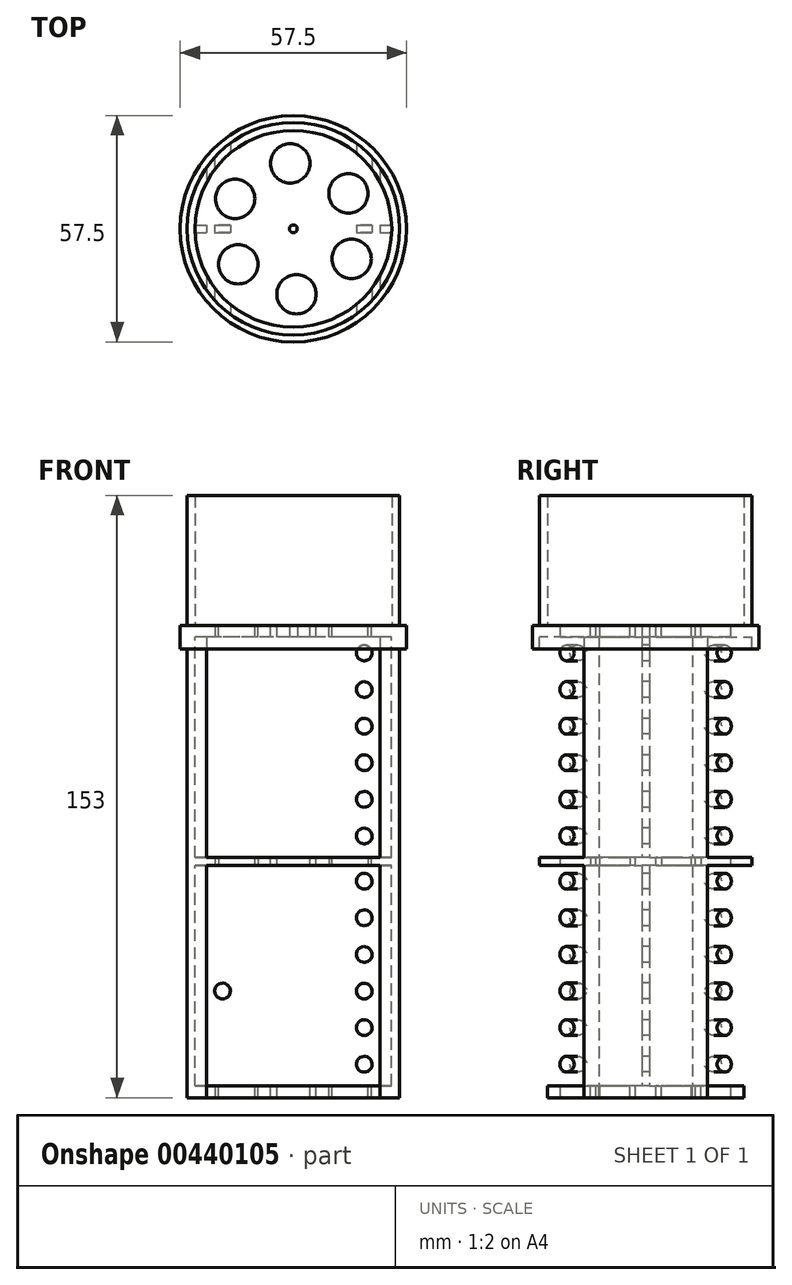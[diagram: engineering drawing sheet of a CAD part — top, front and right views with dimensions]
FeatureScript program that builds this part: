
annotation { "Feature Type Name" : "Feature", "Feature Type Description" : "" }
export const myFeature = defineFeature(function(context is Context, id is Id, definition is map)
    precondition{}
    {
        {
            var Q0;
            Q0=qCreatedBy(makeId("Top.planeOp"),FACE);
            var sketch = newSketch(context, id + "F0", { "sketchPlane" : qUnion([Q0])});
            skCircle(sketch, "E0", {"center": v(0, 0) * mm, "radius": 28.75 * mm});
            skCircle(sketch, "E1", {"center": v(0, 0) * mm, "radius": 27 * mm});
            skCircle(sketch, "E2", {"center": v(0, 0) * mm, "radius": 25 * mm});
            skLineSegment(sketch, "E3", {"start": v(0, 0) * mm, "end": v(28.75, 0) * mm, "construction": true});
            skLineSegment(sketch, "E4", {"start": v(0, 0) * mm, "end": v(-14.37, 24.9) * mm, "construction": true});
            skLineSegment(sketch, "E5", {"start": v(0, 0) * mm, "end": v(-14.38, -24.9) * mm, "construction": true});
            skCircle(sketch, "E6", {"center": v(14, 9) * mm, "radius": 5 * mm});
            skCircle(sketch, "E7", {"center": v(-14, -9) * mm, "radius": 5 * mm});
            skCircle(sketch, "E8.1.0", {"center": v(14.8, -7.62) * mm, "radius": 5 * mm});
            skCircle(sketch, "E8.2.0", {"center": v(0.8, -16.62) * mm, "radius": 5 * mm});
            skCircle(sketch, "E8.4.0", {"center": v(-14.8, 7.62) * mm, "radius": 5 * mm});
            skCircle(sketch, "E8.5.0", {"center": v(-0.8, 16.62) * mm, "radius": 5 * mm});
            skSolve(sketch);
        }
        {
            var Q0;
            Q0=qCreatedBy(makeId("Top.planeOp"),FACE);
            var sketch = newSketch(context, id + "F1", { "sketchPlane" : qUnion([Q0])});
            skArc(sketch, "E9.0.0", {"start": v(-24.98, 1) * mm, "mid": v(-25, 0) * mm, "end": v(-24.98, -1) * mm});
            skLineSegment(sketch, "E10", {"start": v(24.98, 1) * mm, "end": v(-24.98, 1) * mm});
            skLineSegment(sketch, "E11", {"start": v(24.98, -1) * mm, "end": v(-24.98, -1) * mm});
            skArc(sketch, "E12.trimOffspring", {"start": v(24.98, -1) * mm, "mid": v(25, 0) * mm, "end": v(24.98, 1) * mm});
            skSolve(sketch);
        }
        {
            var Q0;
            Q0=qCreatedBy(makeId("Front.planeOp"),FACE);
            var sketch = newSketch(context, id + "F2", { "sketchPlane" : qUnion([Q0])});
            skLineSegment(sketch, "E13", {"start": v(0, 0) * mm, "end": v(25, 0) * mm, "construction": true});
            skLineSegment(sketch, "E14", {"start": v(25, 0) * mm, "end": v(27, 0) * mm, "construction": true});
            skLineSegment(sketch, "E15", {"start": v(27, 0) * mm, "end": v(28.75, 0) * mm, "construction": true});
            skLineSegment(sketch, "E16", {"start": v(25, -10) * mm, "end": v(25, 10) * mm, "construction": true});
            skLineSegment(sketch, "E17", {"start": v(27, -10) * mm, "end": v(27, 10) * mm, "construction": true});
            skLineSegment(sketch, "E18", {"start": v(28.75, -10) * mm, "end": v(28.75, 10) * mm, "construction": true});
            skLineSegment(sketch, "E19", {"start": v(25, 10) * mm, "end": v(25, 105) * mm, "construction": true});
            skLineSegment(sketch, "E20", {"start": v(27, 10) * mm, "end": v(27, 105) * mm, "construction": true});
            skLineSegment(sketch, "E21", {"start": v(25, -10) * mm, "end": v(25, -105) * mm, "construction": true});
            skLineSegment(sketch, "E22", {"start": v(27, -10) * mm, "end": v(27, -105) * mm, "construction": true});
            skLineSegment(sketch, "E23", {"start": v(0, 0) * mm, "end": v(-25, 0) * mm, "construction": true});
            skLineSegment(sketch, "E24", {"start": v(-25, 0) * mm, "end": v(-27, 0) * mm, "construction": true});
            skLineSegment(sketch, "E25", {"start": v(-27, 0) * mm, "end": v(-28.75, 0) * mm, "construction": true});
            skLineSegment(sketch, "E26", {"start": v(0, 0) * mm, "end": v(0, 43) * mm, "construction": true});
            skLineSegment(sketch, "E27", {"start": v(0, 43) * mm, "end": v(0, 45) * mm, "construction": true});
            skLineSegment(sketch, "E28", {"start": v(0, 0) * mm, "end": v(0, -13) * mm, "construction": true});
            skLineSegment(sketch, "E29", {"start": v(0, -13) * mm, "end": v(0, -15) * mm, "construction": true});
            skLineSegment(sketch, "E30", {"start": v(0, 45) * mm, "end": v(0, 101) * mm, "construction": true});
            skLineSegment(sketch, "E31", {"start": v(0, -15) * mm, "end": v(0, -101) * mm, "construction": true});
            skLineSegment(sketch, "E32", {"start": v(0, 101) * mm, "end": v(0, 105) * mm, "construction": true});
            skLineSegment(sketch, "E33", {"start": v(0, -101) * mm, "end": v(0, -105) * mm, "construction": true});
            skLineSegment(sketch, "E34.bottom", {"start": v(-22, 101) * mm, "end": v(22, 101) * mm});
            skLineSegment(sketch, "E34.top", {"start": v(-22, 45) * mm, "end": v(22, 45) * mm});
            skLineSegment(sketch, "E34.left", {"start": v(-22, 101) * mm, "end": v(-22, 45) * mm});
            skLineSegment(sketch, "E34.right", {"start": v(22, 101) * mm, "end": v(22, 45) * mm});
            skLineSegment(sketch, "E35.bottom", {"start": v(-22, 43) * mm, "end": v(22, 43) * mm});
            skLineSegment(sketch, "E35.top", {"start": v(-22, -13) * mm, "end": v(22, -13) * mm});
            skLineSegment(sketch, "E35.left", {"start": v(-22, 43) * mm, "end": v(-22, -13) * mm});
            skLineSegment(sketch, "E35.right", {"start": v(22, 43) * mm, "end": v(22, -13) * mm});
            skLineSegment(sketch, "E36.bottom", {"start": v(-22, -15) * mm, "end": v(22, -15) * mm});
            skLineSegment(sketch, "E36.top", {"start": v(-22, -101) * mm, "end": v(22, -101) * mm});
            skLineSegment(sketch, "E36.left", {"start": v(-22, -15) * mm, "end": v(-22, -101) * mm});
            skLineSegment(sketch, "E36.right", {"start": v(22, -15) * mm, "end": v(22, -101) * mm});
            skLineSegment(sketch, "E37", {"start": v(-22, 10) * mm, "end": v(22, 10) * mm});
            skSolve(sketch);
        }
        {
            var Q0;
            Q0=sQuery(id+"F2.wireOp",VERTEX,"E35.bottom.end");
            var Q1;
            Q1=qCreatedBy(makeId("Top.planeOp"),FACE);
            cPlane(context, id + "F3", {"entities" : qUnion([Q0, Q1]), "cplaneType" : CPlaneType.PLANE_POINT, "offset" : 25 * mm, "width" : 150 * mm, "height" : 150 * mm});
        }
        {
            var Q0;
            Q0=sQuery(id+"F2.wireOp",VERTEX,"E34.bottom.end");
            var Q1;
            Q1=qCreatedBy(id+"F3.planeOp",FACE);
            cPlane(context, id + "F4", {"entities" : qUnion([Q0, Q1]), "cplaneType" : CPlaneType.PLANE_POINT, "offset" : 25 * mm, "width" : 150 * mm, "height" : 150 * mm});
        }
        {
            var Q0;
            Q0=sQuery(id+"F2.wireOp",VERTEX,"E35.right.end");
            var Q1;
            Q1=qCreatedBy(makeId("Top.planeOp"),FACE);
            cPlane(context, id + "F5", {"entities" : qUnion([Q0, Q1]), "cplaneType" : CPlaneType.PLANE_POINT, "offset" : 25 * mm, "width" : 150 * mm, "height" : 150 * mm});
        }
        {
            var Q0;
            Q0=sQuery(id+"F2.wireOp",VERTEX,"E36.top.end");
            var Q1;
            Q1=qCreatedBy(id+"F5.planeOp",FACE);
            cPlane(context, id + "F6", {"entities" : qUnion([Q0, Q1]), "cplaneType" : CPlaneType.PLANE_POINT, "offset" : 25 * mm, "width" : 150 * mm, "height" : 150 * mm});
        }
        {
            var Q0;
            Q0=qCreatedBy(id+"F5.planeOp",FACE);
            var sketch = newSketch(context, id + "F7", { "sketchPlane" : qUnion([Q0])});
            skCircle(sketch, "E38.0", {"center": v(0, 0) * mm, "radius": 25 * mm});
            skLineSegment(sketch, "E39", {"start": v(0, 0) * mm, "end": v(14, 0) * mm, "construction": true});
            skLineSegment(sketch, "E40", {"start": v(14, 0) * mm, "end": v(14, 9) * mm, "construction": true});
            skLineSegment(sketch, "E41", {"start": v(0, 0) * mm, "end": v(-14, 0) * mm, "construction": true});
            skLineSegment(sketch, "E42", {"start": v(-14, 0) * mm, "end": v(-14, -9) * mm, "construction": true});
            skCircle(sketch, "E43", {"center": v(14, 9) * mm, "radius": 5 * mm});
            skCircle(sketch, "E44", {"center": v(-14, -9) * mm, "radius": 5 * mm});
            skSolve(sketch);
        }
        {
            var Q0;
            Q0=qCreatedBy(id+"F3.planeOp",FACE);
            var sketch = newSketch(context, id + "F8", { "sketchPlane" : qUnion([Q0])});
            skCircle(sketch, "E45.0.0", {"center": v(0, 0) * mm, "radius": 25 * mm});
            skCircle(sketch, "E46.0", {"center": v(14, 9) * mm, "radius": 5 * mm});
            skCircle(sketch, "E46.1", {"center": v(-14, -9) * mm, "radius": 5 * mm});
            skSolve(sketch);
        }
        {
            var Q0;
            Q0=qCreatedBy(id+"F4.planeOp",FACE);
            var sketch = newSketch(context, id + "F9", { "sketchPlane" : qUnion([Q0])});
            skCircle(sketch, "E47.0", {"center": v(0, 0) * mm, "radius": 25 * mm});
            skCircle(sketch, "E48", {"center": v(0, 0) * mm, "radius": 1 * mm});
            skCircle(sketch, "E49.0", {"center": v(0, 0) * mm, "radius": 27 * mm});
            skCircle(sketch, "E50.0", {"center": v(0, 0) * mm, "radius": 28.75 * mm});
            skSolve(sketch);
        }
        {
            var Q0;
            Q0=qCreatedBy(makeId("Front.planeOp"),FACE);
            var sketch = newSketch(context, id + "F10", { "sketchPlane" : qUnion([Q0])});
            skLineSegment(sketch, "E51.0.0", {"start": v(-22, 101) * mm, "end": v(-22, 45) * mm});
            skLineSegment(sketch, "E51.0.1", {"start": v(-22, 45) * mm, "end": v(22, 45) * mm});
            skLineSegment(sketch, "E51.0.2", {"start": v(22, 45) * mm, "end": v(22, 101) * mm});
            skLineSegment(sketch, "E51.0.3", {"start": v(22, 101) * mm, "end": v(-22, 101) * mm});
            skLineSegment(sketch, "E51.1.0", {"start": v(-22, 43) * mm, "end": v(-22, 10) * mm});
            skLineSegment(sketch, "E51.1.1", {"start": v(-22, 10) * mm, "end": v(22, 10) * mm});
            skLineSegment(sketch, "E51.1.2", {"start": v(22, 10) * mm, "end": v(22, 43) * mm});
            skLineSegment(sketch, "E51.1.3", {"start": v(22, 43) * mm, "end": v(-22, 43) * mm});
            skLineSegment(sketch, "E51.2.0", {"start": v(-22, 10) * mm, "end": v(-22, -13) * mm});
            skLineSegment(sketch, "E51.2.1", {"start": v(-22, -13) * mm, "end": v(22, -13) * mm});
            skLineSegment(sketch, "E51.2.2", {"start": v(22, -13) * mm, "end": v(22, 10) * mm});
            skLineSegment(sketch, "E51.2.3", {"start": v(22, 10) * mm, "end": v(-22, 10) * mm});
            skLineSegment(sketch, "E51.3.0", {"start": v(-22, -15) * mm, "end": v(-22, -101) * mm});
            skLineSegment(sketch, "E51.3.1", {"start": v(-22, -101) * mm, "end": v(22, -101) * mm});
            skLineSegment(sketch, "E51.3.2", {"start": v(22, -101) * mm, "end": v(22, -15) * mm});
            skLineSegment(sketch, "E51.3.3", {"start": v(22, -15) * mm, "end": v(-22, -15) * mm});
            skCircle(sketch, "E52", {"center": v(-18, 97) * mm, "radius": 2 * mm});
            skCircle(sketch, "E53.1.0.0", {"center": v(-18, 87.7) * mm, "radius": 2 * mm});
            skCircle(sketch, "E53.2.0.0", {"center": v(-18, 78.4) * mm, "radius": 2 * mm});
            skCircle(sketch, "E53.3.0.0", {"center": v(-18, 69.1) * mm, "radius": 2 * mm});
            skCircle(sketch, "E53.4.0.0", {"center": v(-18, 59.8) * mm, "radius": 2 * mm});
            skCircle(sketch, "E53.5.0.0", {"center": v(-18, 50.5) * mm, "radius": 2 * mm});
            skLineSegment(sketch, "E53.direction1", {"start": v(-18, 97) * mm, "end": v(-18, 87.7) * mm, "construction": true});
            skCircle(sketch, "E54", {"center": v(-18, 39) * mm, "radius": 2 * mm});
            skCircle(sketch, "E55.1.0.0", {"center": v(-18, 29.7) * mm, "radius": 2 * mm});
            skCircle(sketch, "E55.2.0.0", {"center": v(-18, 20.4) * mm, "radius": 2 * mm});
            skCircle(sketch, "E55.3.0.0", {"center": v(-18, 11.1) * mm, "radius": 2 * mm});
            skCircle(sketch, "E55.4.0.0", {"center": v(-18, 1.8) * mm, "radius": 2 * mm});
            skCircle(sketch, "E55.5.0.0", {"center": v(-18, -7.5) * mm, "radius": 2 * mm});
            skLineSegment(sketch, "E55.direction1", {"start": v(-18, 39) * mm, "end": v(-18, 29.7) * mm, "construction": true});
            skCircle(sketch, "E56", {"center": v(-18, -19) * mm, "radius": 2 * mm});
            skCircle(sketch, "E57.1.0.0", {"center": v(-18, -30) * mm, "radius": 2 * mm});
            skCircle(sketch, "E57.2.0.0", {"center": v(-18, -41) * mm, "radius": 2 * mm});
            skCircle(sketch, "E57.3.0.0", {"center": v(-18, -52) * mm, "radius": 2 * mm});
            skCircle(sketch, "E57.4.0.0", {"center": v(-18, -63) * mm, "radius": 2 * mm});
            skCircle(sketch, "E57.5.0.0", {"center": v(-18, -74) * mm, "radius": 2 * mm});
            skCircle(sketch, "E57.6.0.0", {"center": v(-18, -85) * mm, "radius": 2 * mm});
            skCircle(sketch, "E57.7.0.0", {"center": v(-18, -96) * mm, "radius": 2 * mm});
            skLineSegment(sketch, "E57.direction1", {"start": v(-18, -19) * mm, "end": v(-18, -30) * mm, "construction": true});
            skCircle(sketch, "E58.MirrorC", {"center": v(18, 97) * mm, "radius": 2 * mm});
            skCircle(sketch, "E59.MirrorC", {"center": v(18, 87.7) * mm, "radius": 2 * mm});
            skCircle(sketch, "E60.MirrorC", {"center": v(18, 78.4) * mm, "radius": 2 * mm});
            skCircle(sketch, "E61.MirrorC", {"center": v(18, 69.1) * mm, "radius": 2 * mm});
            skCircle(sketch, "E62.MirrorC", {"center": v(18, 59.8) * mm, "radius": 2 * mm});
            skCircle(sketch, "E63.MirrorC", {"center": v(18, 50.5) * mm, "radius": 2 * mm});
            skCircle(sketch, "E64.MirrorC", {"center": v(18, 39) * mm, "radius": 2 * mm});
            skCircle(sketch, "E65.MirrorC", {"center": v(18, 29.7) * mm, "radius": 2 * mm});
            skCircle(sketch, "E66.MirrorC", {"center": v(18, 20.4) * mm, "radius": 2 * mm});
            skCircle(sketch, "E67.MirrorC", {"center": v(18, 11.1) * mm, "radius": 2 * mm});
            skCircle(sketch, "E68.MirrorC", {"center": v(18, 1.8) * mm, "radius": 2 * mm});
            skCircle(sketch, "E69.MirrorC", {"center": v(18, -7.5) * mm, "radius": 2 * mm});
            skCircle(sketch, "E70.MirrorC", {"center": v(18, -19) * mm, "radius": 2 * mm});
            skCircle(sketch, "E71.MirrorC", {"center": v(18, -30) * mm, "radius": 2 * mm});
            skCircle(sketch, "E72.MirrorC", {"center": v(18, -41) * mm, "radius": 2 * mm});
            skCircle(sketch, "E73.MirrorC", {"center": v(18, -52) * mm, "radius": 2 * mm});
            skCircle(sketch, "E74.MirrorC", {"center": v(18, -63) * mm, "radius": 2 * mm});
            skCircle(sketch, "E75.MirrorC", {"center": v(18, -74) * mm, "radius": 2 * mm});
            skCircle(sketch, "E76.MirrorC", {"center": v(18, -85) * mm, "radius": 2 * mm});
            skCircle(sketch, "E77.MirrorC", {"center": v(18, -96) * mm, "radius": 2 * mm});
            skLineSegment(sketch, "E78", {"start": v(8, 101) * mm, "end": v(8, 83) * mm});
            skLineSegment(sketch, "E79", {"start": v(8, 83) * mm, "end": v(-8, 83) * mm});
            skLineSegment(sketch, "E80", {"start": v(-8, 83) * mm, "end": v(-8, 101) * mm});
            skLineSegment(sketch, "E81", {"start": v(0, 101) * mm, "end": v(0, 45) * mm, "construction": true});
            skSolve(sketch);
        }
        {
            var Q0;
            Q0=makeQuery(id+"F0.imprint","IMPRINT",FACE,{"disambiguationData":[TD([[makeQuery(id+"F0.imprint","IMPRINT",EDGE,{"derivedFrom":sQuery(id+"F0.wireOp",EDGE,"E1")}),1.0]])]});
            extrude(context, id + "F11", {"entities" : qUnion([Q0]), "depth" : 137 * mm, "offsetDistance" : 25 * mm});
        }
        {
            var Q0;
            Q0=makeQuery(id+"F0.imprint","IMPRINT",FACE,{"disambiguationData":[TD([[makeQuery(id+"F0.imprint","IMPRINT",EDGE,{"derivedFrom":sQuery(id+"F0.wireOp",EDGE,"E1")}),1.0]])]});
            var Q1;
            Q1=makeQuery(id+"F1.imprint","IMPRINT",FACE,{"disambiguationData":[TD([[makeQuery(id+"F1.imprint","IMPRINT",EDGE,{"derivedFrom":sQuery(id+"F1.wireOp",EDGE,"E9.0.0")}),1.0]])]});
            var Q2;
            Q2=qCreatedBy(id+"F5.planeOp",FACE);
            extrude(context, id + "F12", {"entities" : qUnion([Q0, Q1]), "operationType" : NewBodyOperationType.ADD, "endBound" : BoundingType.UP_TO_SURFACE, "oppositeDirection" : true, "depth" : 25 * mm, "endBoundEntityFace" : qUnion([Q2]), "offsetDistance" : 25 * mm});
        }
        {
            var Q0;
            {var subQ1=sQuery(id+"F10.wireOp",EDGE,"E51.0.0");Q0=makeQuery(id+"F10.imprint","IMPRINT",FACE,{"disambiguationData":[TD([[makeQuery(id+"F10.imprint","IMPRINT",EDGE,{"derivedFrom":subQ1}),1.0]])]});}
            var Q1;
            {var subQ0=sQuery(id+"F10.wireOp",EDGE,"E78");Q1=makeQuery(id+"F10.imprint","IMPRINT",FACE,{"disambiguationData":[TD([[makeQuery(id+"F10.imprint","IMPRINT",EDGE,{"derivedFrom":subQ0}),-1.0]])]});}
            var Q2;
            Q2=makeQuery(id+"F10.imprint","IMPRINT",FACE,{"disambiguationData":[TD([[makeQuery(id+"F10.imprint","IMPRINT",EDGE,{"derivedFrom":sQuery(id+"F10.wireOp",EDGE,"E59.MirrorC")}),-1.0]])]});
            var Q3;
            Q3=makeQuery(id+"F10.imprint","IMPRINT",FACE,{"disambiguationData":[TD([[makeQuery(id+"F10.imprint","IMPRINT",EDGE,{"derivedFrom":sQuery(id+"F10.wireOp",EDGE,"E53.1.0.0")}),1.0]])]});
            var Q4;
            Q4=makeQuery(id+"F10.imprint","IMPRINT",FACE,{"disambiguationData":[TD([[makeQuery(id+"F10.imprint","IMPRINT",EDGE,{"derivedFrom":sQuery(id+"F10.wireOp",EDGE,"E52")}),1.0]])]});
            var Q5;
            Q5=makeQuery(id+"F10.imprint","IMPRINT",FACE,{"disambiguationData":[TD([[makeQuery(id+"F10.imprint","IMPRINT",EDGE,{"derivedFrom":sQuery(id+"F10.wireOp",EDGE,"E61.MirrorC")}),-1.0]])]});
            var Q6;
            Q6=makeQuery(id+"F10.imprint","IMPRINT",FACE,{"disambiguationData":[TD([[makeQuery(id+"F10.imprint","IMPRINT",EDGE,{"derivedFrom":sQuery(id+"F10.wireOp",EDGE,"E62.MirrorC")}),-1.0]])]});
            var Q7;
            Q7=makeQuery(id+"F10.imprint","IMPRINT",FACE,{"disambiguationData":[TD([[makeQuery(id+"F10.imprint","IMPRINT",EDGE,{"derivedFrom":sQuery(id+"F10.wireOp",EDGE,"E53.3.0.0")}),1.0]])]});
            var Q8;
            Q8=makeQuery(id+"F10.imprint","IMPRINT",FACE,{"disambiguationData":[TD([[makeQuery(id+"F10.imprint","IMPRINT",EDGE,{"derivedFrom":sQuery(id+"F10.wireOp",EDGE,"E53.2.0.0")}),1.0]])]});
            var Q9;
            Q9=makeQuery(id+"F10.imprint","IMPRINT",FACE,{"disambiguationData":[TD([[makeQuery(id+"F10.imprint","IMPRINT",EDGE,{"derivedFrom":sQuery(id+"F10.wireOp",EDGE,"E53.4.0.0")}),1.0]])]});
            var Q10;
            Q10=makeQuery(id+"F10.imprint","IMPRINT",FACE,{"disambiguationData":[TD([[makeQuery(id+"F10.imprint","IMPRINT",EDGE,{"derivedFrom":sQuery(id+"F10.wireOp",EDGE,"E53.5.0.0")}),1.0]])]});
            var Q11;
            Q11=makeQuery(id+"F10.imprint","IMPRINT",FACE,{"disambiguationData":[TD([[makeQuery(id+"F10.imprint","IMPRINT",EDGE,{"derivedFrom":sQuery(id+"F10.wireOp",EDGE,"E60.MirrorC")}),-1.0]])]});
            var Q12;
            Q12=makeQuery(id+"F10.imprint","IMPRINT",FACE,{"disambiguationData":[TD([[makeQuery(id+"F10.imprint","IMPRINT",EDGE,{"derivedFrom":sQuery(id+"F10.wireOp",EDGE,"E63.MirrorC")}),-1.0]])]});
            var Q13;
            Q13=makeQuery(id+"F10.imprint","IMPRINT",FACE,{"disambiguationData":[TD([[makeQuery(id+"F10.imprint","IMPRINT",EDGE,{"derivedFrom":sQuery(id+"F10.wireOp",EDGE,"E58.MirrorC")}),-1.0]])]});
            var Q14;
            {var subQ7=sQuery(id+"F10.wireOp",EDGE,"E51.2.0");Q14=makeQuery(id+"F10.imprint","IMPRINT",FACE,{"disambiguationData":[TD([[makeQuery(id+"F10.imprint","IMPRINT",EDGE,{"derivedFrom":subQ7}),1.0]])]});}
            var Q15;
            {var subQ4=sQuery(id+"F10.wireOp",EDGE,"E51.1.0");Q15=makeQuery(id+"F10.imprint","IMPRINT",FACE,{"disambiguationData":[TD([[makeQuery(id+"F10.imprint","IMPRINT",EDGE,{"derivedFrom":subQ4}),1.0]])]});}
            var Q16;
            Q16=makeQuery(id+"F10.imprint","IMPRINT",FACE,{"disambiguationData":[TD([[makeQuery(id+"F10.imprint","IMPRINT",EDGE,{"derivedFrom":sQuery(id+"F10.wireOp",EDGE,"E54")}),1.0]])]});
            var Q17;
            Q17=makeQuery(id+"F10.imprint","IMPRINT",FACE,{"disambiguationData":[TD([[makeQuery(id+"F10.imprint","IMPRINT",EDGE,{"derivedFrom":sQuery(id+"F10.wireOp",EDGE,"E55.5.0.0")}),1.0]])]});
            var Q18;
            Q18=makeQuery(id+"F10.imprint","IMPRINT",FACE,{"disambiguationData":[TD([[makeQuery(id+"F10.imprint","IMPRINT",EDGE,{"derivedFrom":sQuery(id+"F10.wireOp",EDGE,"E66.MirrorC")}),-1.0]])]});
            var Q19;
            Q19=makeQuery(id+"F10.imprint","IMPRINT",FACE,{"disambiguationData":[TD([[makeQuery(id+"F10.imprint","IMPRINT",EDGE,{"derivedFrom":sQuery(id+"F10.wireOp",EDGE,"E55.1.0.0")}),1.0]])]});
            var Q20;
            {var subQ0=sQuery(id+"F10.wireOp",EDGE,"E67.MirrorC");var subQ1=sQuery(id+"F10.wireOp",EDGE,"E51.2.3");var subQ2=makeQuery(id+"F10.imprint","INTERSECT",VERTEX,{"disambiguationData":[OD(0.0)],"derivedFrom":[subQ1,subQ0]});Q20=makeQuery(id+"F10.imprint","IMPRINT",FACE,{"disambiguationData":[TD([[makeQuery(id+"F10.imprint","IMPRINT",EDGE,{"disambiguationData":[TD([[subQ2,-1.0]])],"derivedFrom":subQ1}),1.0]])]});}
            var Q21;
            Q21=makeQuery(id+"F10.imprint","IMPRINT",FACE,{"disambiguationData":[TD([[makeQuery(id+"F10.imprint","IMPRINT",EDGE,{"derivedFrom":sQuery(id+"F10.wireOp",EDGE,"E69.MirrorC")}),-1.0]])]});
            var Q22;
            {var subQ0=sQuery(id+"F10.wireOp",EDGE,"E67.MirrorC");var subQ1=sQuery(id+"F10.wireOp",EDGE,"E51.2.3");var subQ2=makeQuery(id+"F10.imprint","INTERSECT",VERTEX,{"disambiguationData":[OD(0.0)],"derivedFrom":[subQ1,subQ0]});Q22=makeQuery(id+"F10.imprint","IMPRINT",FACE,{"disambiguationData":[TD([[makeQuery(id+"F10.imprint","IMPRINT",EDGE,{"disambiguationData":[TD([[subQ2,-1.0]])],"derivedFrom":subQ1}),-1.0]])]});}
            var Q23;
            Q23=makeQuery(id+"F10.imprint","IMPRINT",FACE,{"disambiguationData":[TD([[makeQuery(id+"F10.imprint","IMPRINT",EDGE,{"derivedFrom":sQuery(id+"F10.wireOp",EDGE,"E55.2.0.0")}),1.0]])]});
            var Q24;
            Q24=makeQuery(id+"F10.imprint","IMPRINT",FACE,{"disambiguationData":[TD([[makeQuery(id+"F10.imprint","IMPRINT",EDGE,{"derivedFrom":sQuery(id+"F10.wireOp",EDGE,"E68.MirrorC")}),-1.0]])]});
            var Q25;
            {var subQ0=sQuery(id+"F10.wireOp",EDGE,"E55.3.0.0");var subQ1=sQuery(id+"F10.wireOp",EDGE,"E51.2.3");var subQ2=makeQuery(id+"F10.imprint","INTERSECT",VERTEX,{"disambiguationData":[OD(0.0)],"derivedFrom":[subQ1,subQ0]});Q25=makeQuery(id+"F10.imprint","IMPRINT",FACE,{"disambiguationData":[TD([[makeQuery(id+"F10.imprint","IMPRINT",EDGE,{"disambiguationData":[TD([[subQ2,-1.0]])],"derivedFrom":subQ1}),-1.0]])]});}
            var Q26;
            Q26=makeQuery(id+"F10.imprint","IMPRINT",FACE,{"disambiguationData":[TD([[makeQuery(id+"F10.imprint","IMPRINT",EDGE,{"derivedFrom":sQuery(id+"F10.wireOp",EDGE,"E64.MirrorC")}),-1.0]])]});
            var Q27;
            {var subQ0=sQuery(id+"F10.wireOp",EDGE,"E55.3.0.0");var subQ1=sQuery(id+"F10.wireOp",EDGE,"E51.2.3");var subQ2=makeQuery(id+"F10.imprint","INTERSECT",VERTEX,{"disambiguationData":[OD(0.0)],"derivedFrom":[subQ1,subQ0]});Q27=makeQuery(id+"F10.imprint","IMPRINT",FACE,{"disambiguationData":[TD([[makeQuery(id+"F10.imprint","IMPRINT",EDGE,{"disambiguationData":[TD([[subQ2,-1.0]])],"derivedFrom":subQ1}),1.0]])]});}
            var Q28;
            Q28=makeQuery(id+"F10.imprint","IMPRINT",FACE,{"disambiguationData":[TD([[makeQuery(id+"F10.imprint","IMPRINT",EDGE,{"derivedFrom":sQuery(id+"F10.wireOp",EDGE,"E65.MirrorC")}),-1.0]])]});
            var Q29;
            Q29=makeQuery(id+"F10.imprint","IMPRINT",FACE,{"disambiguationData":[TD([[makeQuery(id+"F10.imprint","IMPRINT",EDGE,{"derivedFrom":sQuery(id+"F10.wireOp",EDGE,"E55.4.0.0")}),1.0]])]});
            extrude(context, id + "F13", {"entities" : qUnion([Q0, Q1, Q2, Q3, Q4, Q5, Q6, Q7, Q8, Q9, Q10, Q11, Q12, Q13, Q14, Q15, Q16, Q17, Q18, Q19, Q20, Q21, Q22, Q23, Q24, Q25, Q26, Q27, Q28, Q29]), "operationType" : NewBodyOperationType.REMOVE, "endBound" : BoundingType.SYMMETRIC, "oppositeDirection" : true, "depth" : 60 * mm, "offsetDistance" : 25 * mm});
        }
        {
            var Q0;
            Q0=makeQuery(id+"F1.imprint","IMPRINT",FACE,{"disambiguationData":[TD([[makeQuery(id+"F1.imprint","IMPRINT",EDGE,{"derivedFrom":sQuery(id+"F1.wireOp",EDGE,"E9.0.0")}),1.0]])]});
            var Q1;
            Q1=qCreatedBy(id+"F5.planeOp",FACE);
            extrude(context, id + "F14", {"entities" : qUnion([Q0]), "operationType" : NewBodyOperationType.ADD, "endBound" : BoundingType.UP_TO_SURFACE, "oppositeDirection" : true, "depth" : 25 * mm, "endBoundEntityFace" : qUnion([Q1]), "offsetDistance" : 25 * mm});
        }
        {
            var Q0;
            Q0=makeQuery(id+"F1.imprint","IMPRINT",FACE,{"disambiguationData":[TD([[makeQuery(id+"F1.imprint","IMPRINT",EDGE,{"derivedFrom":sQuery(id+"F1.wireOp",EDGE,"E9.0.0")}),1.0]])]});
            var Q1;
            Q1=qCreatedBy(id+"F4.planeOp",FACE);
            extrude(context, id + "F15", {"entities" : qUnion([Q0]), "operationType" : NewBodyOperationType.ADD, "endBound" : BoundingType.UP_TO_SURFACE, "depth" : 25 * mm, "endBoundEntityFace" : qUnion([Q1]), "offsetDistance" : 25 * mm});
        }
        {
            var Q0;
            Q0=makeQuery(id+"F8.imprint","IMPRINT",FACE,{"disambiguationData":[TD([[makeQuery(id+"F8.imprint","IMPRINT",EDGE,{"derivedFrom":sQuery(id+"F8.wireOp",EDGE,"E45.0.0")}),1.0]])]});
            extrude(context, id + "F16", {"entities" : qUnion([Q0]), "operationType" : NewBodyOperationType.ADD, "depth" : 2 * mm, "offsetDistance" : 25 * mm});
        }
        {
            var Q0;
            Q0=makeQuery(id+"F7.imprint","IMPRINT",FACE,{"disambiguationData":[TD([[makeQuery(id+"F7.imprint","IMPRINT",EDGE,{"derivedFrom":sQuery(id+"F7.wireOp",EDGE,"E38.0")}),1.0]])]});
            var Q1;
            {var subQ0=sQuery(id+"F1.wireOp",EDGE,"E12.trimOffspring");var subQ1=sQuery(id+"F1.wireOp",EDGE,"E11");var subQ2=sQuery(id+"F1.wireOp",EDGE,"E10");var subQ3=sQuery(id+"F1.wireOp",EDGE,"E9.0.0");var subQ4=sQuery(id+"F0.wireOp",EDGE,"E2");var subQ6=sQuery(id+"F0.wireOp",EDGE,"E1");var subQ12=makeQuery(id+"F12.boolean.opBoolean","MERGE",FACE,{"derivedFrom":[makeQuery(id+"F12.opExtrude","CAP_FACE",FACE,{"disambiguationData":[OSD([subQ6,subQ4])],"isStart":false}),makeQuery(id+"F12.opExtrude","CAP_FACE",FACE,{"disambiguationData":[OSD([subQ3,subQ2,subQ1,subQ0])],"isStart":false})]});Q1=makeQuery(id+"F14.boolean.opBoolean","MERGE",FACE,{"derivedFrom":[makeQuery(id+"F13.boolean.opBoolean","SPLIT",FACE,{"disambiguationData":[TD([makeQuery(id+"F13.opExtrude","SWEPT_FACE",FACE,{"disambiguationData":[OSD([sQuery(id+"F10.wireOp",EDGE,"E51.1.0"),sQuery(id+"F10.wireOp",EDGE,"E51.2.0")])]})])],"derivedFrom":subQ12}),makeQuery(id+"F13.boolean.opBoolean","SPLIT",FACE,{"disambiguationData":[TD([makeQuery(id+"F13.opExtrude","SWEPT_FACE",FACE,{"disambiguationData":[OSD([sQuery(id+"F10.wireOp",EDGE,"E51.1.2"),sQuery(id+"F10.wireOp",EDGE,"E51.2.2")])]})])],"derivedFrom":subQ12}),makeQuery(id+"F14.opExtrude","CAP_FACE",FACE,{"disambiguationData":[OSD([subQ3,subQ2,subQ1,subQ0])],"isStart":false})]});}
            var Q2;
            {var subQ0=sQuery(id+"F1.wireOp",EDGE,"E12.trimOffspring");var subQ1=sQuery(id+"F1.wireOp",EDGE,"E11");var subQ2=sQuery(id+"F1.wireOp",EDGE,"E10");var subQ3=sQuery(id+"F1.wireOp",EDGE,"E9.0.0");var subQ4=sQuery(id+"F0.wireOp",EDGE,"E2");var subQ6=sQuery(id+"F0.wireOp",EDGE,"E1");var subQ12=makeQuery(id+"F12.boolean.opBoolean","MERGE",FACE,{"derivedFrom":[makeQuery(id+"F12.opExtrude","CAP_FACE",FACE,{"disambiguationData":[OSD([subQ6,subQ4])],"isStart":false}),makeQuery(id+"F12.opExtrude","CAP_FACE",FACE,{"disambiguationData":[OSD([subQ3,subQ2,subQ1,subQ0])],"isStart":false})]});Q2=makeQuery(id+"F14.boolean.opBoolean","MERGE",FACE,{"derivedFrom":[makeQuery(id+"F13.boolean.opBoolean","SPLIT",FACE,{"disambiguationData":[TD([makeQuery(id+"F13.opExtrude","SWEPT_FACE",FACE,{"disambiguationData":[OSD([sQuery(id+"F10.wireOp",EDGE,"E51.1.0"),sQuery(id+"F10.wireOp",EDGE,"E51.2.0")])]})])],"derivedFrom":subQ12}),makeQuery(id+"F13.boolean.opBoolean","SPLIT",FACE,{"disambiguationData":[TD([makeQuery(id+"F13.opExtrude","SWEPT_FACE",FACE,{"disambiguationData":[OSD([sQuery(id+"F10.wireOp",EDGE,"E51.1.2"),sQuery(id+"F10.wireOp",EDGE,"E51.2.2")])]})])],"derivedFrom":subQ12}),makeQuery(id+"F14.opExtrude","CAP_FACE",FACE,{"disambiguationData":[OSD([subQ3,subQ2,subQ1,subQ0])],"isStart":false})]});}
            extrude(context, id + "F17", {"entities" : qUnion([Q0, Q1, Q2]), "operationType" : NewBodyOperationType.ADD, "oppositeDirection" : true, "depth" : 3 * mm, "offsetDistance" : 25 * mm});
        }
        {
            var Q0;
            Q0=makeQuery(id+"F9.imprint","IMPRINT",FACE,{"disambiguationData":[TD([[makeQuery(id+"F9.imprint","IMPRINT",EDGE,{"derivedFrom":sQuery(id+"F9.wireOp",EDGE,"E47.0")}),1.0]])]});
            var Q1;
            Q1=makeQuery(id+"F9.imprint","IMPRINT",FACE,{"disambiguationData":[TD([[makeQuery(id+"F9.imprint","IMPRINT",EDGE,{"derivedFrom":sQuery(id+"F9.wireOp",EDGE,"E48")}),1.0]])]});
            extrude(context, id + "F18", {"entities" : qUnion([Q0, Q1]), "operationType" : NewBodyOperationType.ADD, "depth" : 3 * mm, "offsetDistance" : 25 * mm});
        }
        {
            var Q0;
            Q0=makeQuery(id+"F0.imprint","IMPRINT",FACE,{"disambiguationData":[TD([[makeQuery(id+"F0.imprint","IMPRINT",EDGE,{"derivedFrom":sQuery(id+"F0.wireOp",EDGE,"E8.2.0")}),1.0]])]});
            var Q1;
            Q1=makeQuery(id+"F0.imprint","IMPRINT",FACE,{"disambiguationData":[TD([[makeQuery(id+"F0.imprint","IMPRINT",EDGE,{"derivedFrom":sQuery(id+"F0.wireOp",EDGE,"E7")}),1.0]])]});
            var Q2;
            Q2=makeQuery(id+"F0.imprint","IMPRINT",FACE,{"disambiguationData":[TD([[makeQuery(id+"F0.imprint","IMPRINT",EDGE,{"derivedFrom":sQuery(id+"F0.wireOp",EDGE,"E8.1.0")}),1.0]])]});
            var Q3;
            Q3=makeQuery(id+"F0.imprint","IMPRINT",FACE,{"disambiguationData":[TD([[makeQuery(id+"F0.imprint","IMPRINT",EDGE,{"derivedFrom":sQuery(id+"F0.wireOp",EDGE,"E8.4.0")}),1.0]])]});
            var Q4;
            Q4=makeQuery(id+"F0.imprint","IMPRINT",FACE,{"disambiguationData":[TD([[makeQuery(id+"F0.imprint","IMPRINT",EDGE,{"derivedFrom":sQuery(id+"F0.wireOp",EDGE,"E8.5.0")}),1.0]])]});
            var Q5;
            Q5=makeQuery(id+"F0.imprint","IMPRINT",FACE,{"disambiguationData":[TD([[makeQuery(id+"F0.imprint","IMPRINT",EDGE,{"derivedFrom":sQuery(id+"F0.wireOp",EDGE,"E6")}),1.0]])]});
            extrude(context, id + "F19", {"entities" : qUnion([Q0, Q1, Q2, Q3, Q4, Q5]), "operationType" : NewBodyOperationType.REMOVE, "endBound" : BoundingType.THROUGH_ALL, "oppositeDirection" : true, "depth" : 25 * mm, "offsetDistance" : 25 * mm, "hasSecondDirection" : true, "secondDirectionBound" : SecondDirectionBoundingType.THROUGH_ALL, "secondDirectionOppositeDirection" : false, "secondDirectionDepth" : 25 * mm});
        }
        {
            var Q0;
            Q0=makeQuery(id+"F10.imprint","IMPRINT",FACE,{"disambiguationData":[TD([[makeQuery(id+"F10.imprint","IMPRINT",EDGE,{"derivedFrom":sQuery(id+"F10.wireOp",EDGE,"E52")}),1.0]])]});
            var Q1;
            Q1=makeQuery(id+"F10.imprint","IMPRINT",FACE,{"disambiguationData":[TD([[makeQuery(id+"F10.imprint","IMPRINT",EDGE,{"derivedFrom":sQuery(id+"F10.wireOp",EDGE,"E53.1.0.0")}),1.0]])]});
            var Q2;
            Q2=makeQuery(id+"F10.imprint","IMPRINT",FACE,{"disambiguationData":[TD([[makeQuery(id+"F10.imprint","IMPRINT",EDGE,{"derivedFrom":sQuery(id+"F10.wireOp",EDGE,"E53.2.0.0")}),1.0]])]});
            var Q3;
            Q3=makeQuery(id+"F10.imprint","IMPRINT",FACE,{"disambiguationData":[TD([[makeQuery(id+"F10.imprint","IMPRINT",EDGE,{"derivedFrom":sQuery(id+"F10.wireOp",EDGE,"E53.3.0.0")}),1.0]])]});
            var Q4;
            Q4=makeQuery(id+"F10.imprint","IMPRINT",FACE,{"disambiguationData":[TD([[makeQuery(id+"F10.imprint","IMPRINT",EDGE,{"derivedFrom":sQuery(id+"F10.wireOp",EDGE,"E53.4.0.0")}),1.0]])]});
            var Q5;
            Q5=makeQuery(id+"F10.imprint","IMPRINT",FACE,{"disambiguationData":[TD([[makeQuery(id+"F10.imprint","IMPRINT",EDGE,{"derivedFrom":sQuery(id+"F10.wireOp",EDGE,"E53.5.0.0")}),1.0]])]});
            var Q6;
            Q6=makeQuery(id+"F10.imprint","IMPRINT",FACE,{"disambiguationData":[TD([[makeQuery(id+"F10.imprint","IMPRINT",EDGE,{"derivedFrom":sQuery(id+"F10.wireOp",EDGE,"E58.MirrorC")}),-1.0]])]});
            var Q7;
            Q7=makeQuery(id+"F10.imprint","IMPRINT",FACE,{"disambiguationData":[TD([[makeQuery(id+"F10.imprint","IMPRINT",EDGE,{"derivedFrom":sQuery(id+"F10.wireOp",EDGE,"E59.MirrorC")}),-1.0]])]});
            var Q8;
            Q8=makeQuery(id+"F10.imprint","IMPRINT",FACE,{"disambiguationData":[TD([[makeQuery(id+"F10.imprint","IMPRINT",EDGE,{"derivedFrom":sQuery(id+"F10.wireOp",EDGE,"E60.MirrorC")}),-1.0]])]});
            var Q9;
            Q9=makeQuery(id+"F10.imprint","IMPRINT",FACE,{"disambiguationData":[TD([[makeQuery(id+"F10.imprint","IMPRINT",EDGE,{"derivedFrom":sQuery(id+"F10.wireOp",EDGE,"E61.MirrorC")}),-1.0]])]});
            var Q10;
            Q10=makeQuery(id+"F10.imprint","IMPRINT",FACE,{"disambiguationData":[TD([[makeQuery(id+"F10.imprint","IMPRINT",EDGE,{"derivedFrom":sQuery(id+"F10.wireOp",EDGE,"E62.MirrorC")}),-1.0]])]});
            var Q11;
            Q11=makeQuery(id+"F10.imprint","IMPRINT",FACE,{"disambiguationData":[TD([[makeQuery(id+"F10.imprint","IMPRINT",EDGE,{"derivedFrom":sQuery(id+"F10.wireOp",EDGE,"E63.MirrorC")}),-1.0]])]});
            var Q12;
            Q12=makeQuery(id+"F10.imprint","IMPRINT",FACE,{"disambiguationData":[TD([[makeQuery(id+"F10.imprint","IMPRINT",EDGE,{"derivedFrom":sQuery(id+"F10.wireOp",EDGE,"E54")}),1.0]])]});
            var Q13;
            Q13=makeQuery(id+"F10.imprint","IMPRINT",FACE,{"disambiguationData":[TD([[makeQuery(id+"F10.imprint","IMPRINT",EDGE,{"derivedFrom":sQuery(id+"F10.wireOp",EDGE,"E55.1.0.0")}),1.0]])]});
            var Q14;
            Q14=makeQuery(id+"F10.imprint","IMPRINT",FACE,{"disambiguationData":[TD([[makeQuery(id+"F10.imprint","IMPRINT",EDGE,{"derivedFrom":sQuery(id+"F10.wireOp",EDGE,"E55.2.0.0")}),1.0]])]});
            var Q15;
            {var subQ0=sQuery(id+"F10.wireOp",EDGE,"E55.3.0.0");var subQ1=sQuery(id+"F10.wireOp",EDGE,"E51.2.3");var subQ2=makeQuery(id+"F10.imprint","INTERSECT",VERTEX,{"disambiguationData":[OD(0.0)],"derivedFrom":[subQ1,subQ0]});Q15=makeQuery(id+"F10.imprint","IMPRINT",FACE,{"disambiguationData":[TD([[makeQuery(id+"F10.imprint","IMPRINT",EDGE,{"disambiguationData":[TD([[subQ2,-1.0]])],"derivedFrom":subQ1}),-1.0]])]});}
            var Q16;
            {var subQ0=sQuery(id+"F10.wireOp",EDGE,"E55.3.0.0");var subQ1=sQuery(id+"F10.wireOp",EDGE,"E51.2.3");var subQ2=makeQuery(id+"F10.imprint","INTERSECT",VERTEX,{"disambiguationData":[OD(0.0)],"derivedFrom":[subQ1,subQ0]});Q16=makeQuery(id+"F10.imprint","IMPRINT",FACE,{"disambiguationData":[TD([[makeQuery(id+"F10.imprint","IMPRINT",EDGE,{"disambiguationData":[TD([[subQ2,-1.0]])],"derivedFrom":subQ1}),1.0]])]});}
            var Q17;
            Q17=makeQuery(id+"F10.imprint","IMPRINT",FACE,{"disambiguationData":[TD([[makeQuery(id+"F10.imprint","IMPRINT",EDGE,{"derivedFrom":sQuery(id+"F10.wireOp",EDGE,"E55.4.0.0")}),1.0]])]});
            var Q18;
            Q18=makeQuery(id+"F10.imprint","IMPRINT",FACE,{"disambiguationData":[TD([[makeQuery(id+"F10.imprint","IMPRINT",EDGE,{"derivedFrom":sQuery(id+"F10.wireOp",EDGE,"E64.MirrorC")}),-1.0]])]});
            var Q19;
            Q19=makeQuery(id+"F10.imprint","IMPRINT",FACE,{"disambiguationData":[TD([[makeQuery(id+"F10.imprint","IMPRINT",EDGE,{"derivedFrom":sQuery(id+"F10.wireOp",EDGE,"E65.MirrorC")}),-1.0]])]});
            var Q20;
            Q20=makeQuery(id+"F10.imprint","IMPRINT",FACE,{"disambiguationData":[TD([[makeQuery(id+"F10.imprint","IMPRINT",EDGE,{"derivedFrom":sQuery(id+"F10.wireOp",EDGE,"E66.MirrorC")}),-1.0]])]});
            var Q21;
            {var subQ0=sQuery(id+"F10.wireOp",EDGE,"E67.MirrorC");var subQ1=sQuery(id+"F10.wireOp",EDGE,"E51.2.3");var subQ2=makeQuery(id+"F10.imprint","INTERSECT",VERTEX,{"disambiguationData":[OD(0.0)],"derivedFrom":[subQ1,subQ0]});Q21=makeQuery(id+"F10.imprint","IMPRINT",FACE,{"disambiguationData":[TD([[makeQuery(id+"F10.imprint","IMPRINT",EDGE,{"disambiguationData":[TD([[subQ2,-1.0]])],"derivedFrom":subQ1}),-1.0]])]});}
            var Q22;
            {var subQ0=sQuery(id+"F10.wireOp",EDGE,"E67.MirrorC");var subQ1=sQuery(id+"F10.wireOp",EDGE,"E51.2.3");var subQ2=makeQuery(id+"F10.imprint","INTERSECT",VERTEX,{"disambiguationData":[OD(0.0)],"derivedFrom":[subQ1,subQ0]});Q22=makeQuery(id+"F10.imprint","IMPRINT",FACE,{"disambiguationData":[TD([[makeQuery(id+"F10.imprint","IMPRINT",EDGE,{"disambiguationData":[TD([[subQ2,-1.0]])],"derivedFrom":subQ1}),1.0]])]});}
            var Q23;
            Q23=makeQuery(id+"F10.imprint","IMPRINT",FACE,{"disambiguationData":[TD([[makeQuery(id+"F10.imprint","IMPRINT",EDGE,{"derivedFrom":sQuery(id+"F10.wireOp",EDGE,"E68.MirrorC")}),-1.0]])]});
            var Q24;
            Q24=makeQuery(id+"F10.imprint","IMPRINT",FACE,{"disambiguationData":[TD([[makeQuery(id+"F10.imprint","IMPRINT",EDGE,{"derivedFrom":sQuery(id+"F10.wireOp",EDGE,"E69.MirrorC")}),-1.0]])]});
            var Q25;
            Q25=makeQuery(id+"F10.imprint","IMPRINT",FACE,{"disambiguationData":[TD([[makeQuery(id+"F10.imprint","IMPRINT",EDGE,{"derivedFrom":sQuery(id+"F10.wireOp",EDGE,"E55.5.0.0")}),1.0]])]});
            var Q26;
            {var subQ0=sQuery(id+"F10.wireOp",EDGE,"E78");Q26=makeQuery(id+"F10.imprint","IMPRINT",FACE,{"disambiguationData":[TD([[makeQuery(id+"F10.imprint","IMPRINT",EDGE,{"derivedFrom":subQ0}),-1.0]])]});}
            extrude(context, id + "F20", {"entities" : qUnion([Q0, Q1, Q2, Q3, Q4, Q5, Q6, Q7, Q8, Q9, Q10, Q11, Q12, Q13, Q14, Q15, Q16, Q17, Q18, Q19, Q20, Q21, Q22, Q23, Q24, Q25, Q26]), "operationType" : NewBodyOperationType.REMOVE, "endBound" : BoundingType.SYMMETRIC, "oppositeDirection" : true, "depth" : 3 * mm, "offsetDistance" : 25 * mm});
        }
        {
            var Q0;
            Q0=makeQuery(id+"F9.imprint","IMPRINT",FACE,{"disambiguationData":[TD([[makeQuery(id+"F9.imprint","IMPRINT",EDGE,{"derivedFrom":sQuery(id+"F9.wireOp",EDGE,"E49.0")}),-1.0]])]});
            extrude(context, id + "F21", {"entities" : qUnion([Q0]), "operationType" : NewBodyOperationType.ADD, "endBound" : BoundingType.SYMMETRIC, "oppositeDirection" : true, "depth" : 6 * mm, "offsetDistance" : 25 * mm});
        }
        {
            var Q0;
            Q0=makeQuery(id+"F9.imprint","IMPRINT",FACE,{"disambiguationData":[TD([[makeQuery(id+"F9.imprint","IMPRINT",EDGE,{"derivedFrom":sQuery(id+"F9.wireOp",EDGE,"E48")}),1.0]])]});
            extrude(context, id + "F22", {"entities" : qUnion([Q0]), "operationType" : NewBodyOperationType.REMOVE, "endBound" : BoundingType.THROUGH_ALL, "depth" : 25 * mm, "offsetDistance" : 25 * mm});
        }
    });
